# Revit family: M_Plug Valve - 3 Way - Lever Handle - 50-100 mm
name_source: partatom
category: Pipe Accessories
revit_build: Autodesk Revit MEP 2014 (Build: 20130308_1515(x64)
units: mm (PartAtom-declared; Revit-internal decimal feet)

## types (4) — shared parameters
Valve Material = PVC, Green

## per-type parameters (varying)
| type | Axis Height | Flange Diameter | Flange Radius | H2 | H3 | Height 1 | Height 2 | Height 3 | K Coefficient | Length 1 | Length 2 | Lever Length | Nominal Radius | Open Height | Outside Diameter | Outside Radius | Radius 1 | Valve Length | Width 1 |
| 50 mm | 114 mm  [stored 0.374016 ft] | 152 mm  [stored 0.498688 ft] | 76 mm  [stored 0.249344 ft] | 119 mm | 36 mm | 76 mm  [stored 0.249344 ft] | 55 mm  [stored 0.180446 ft] | 28 mm | 3.48 | 89 mm  [stored 0.291995 ft] | 103 mm | 457 mm  [stored 1.49934 ft] | 25 mm | 130 mm  [stored 0.426509 ft] | 55 mm | 28 mm | 26 mm | 178 mm  [stored 0.58399 ft] | 38 mm |
| 65 mm | 130 mm  [stored 0.426509 ft] | 178 mm  [stored 0.58399 ft] | 89 mm  [stored 0.291995 ft] | 135 mm | 41 mm | 89 mm  [stored 0.291995 ft] | 72 mm | 36 mm | 3.59 | 102 mm | 117 mm | 610 mm  [stored 2.00131 ft] | 33 mm | 145 mm  [stored 0.475722 ft] | 72 mm | 36 mm | 29 mm | 203 mm  [stored 0.66601 ft] | 49 mm |
| 80 mm | 130 mm  [stored 0.426509 ft] | 191 mm  [stored 0.62664 ft] | 96 mm | 135 mm | 41 mm | 95 mm | 88 mm | 44 mm | 8.76 | 102 mm | 117 mm | 610 mm  [stored 2.00131 ft] | 40 mm | 145 mm  [stored 0.475722 ft] | 88 mm | 44 mm | 29 mm | 203 mm  [stored 0.66601 ft] | 60 mm  [stored 0.19685 ft] |
| 100 mm | 152 mm  [stored 0.498688 ft] | 229 mm | 115 mm | 153 mm | 46 mm | 114 mm  [stored 0.374016 ft] | 110 mm  [stored 0.360892 ft] | 55 mm  [stored 0.180446 ft] | 8.51 | 115 mm | 132 mm | 762 mm  [stored 2.5 ft] | 50 mm | 178 mm  [stored 0.58399 ft] | 110 mm | 55 mm  [stored 0.180446 ft] | 33 mm | 229 mm | 75 mm  [stored 0.246063 ft] |

note: column(s) folded — value = type name in every type: Nominal Diameter

note: [stored X ft] marks values corroborated as IEEE doubles in the binary element streams (Revit-internal decimal feet)

## geometry (parser evidence)
native form markers: Blend x2, Sweep x1
no freeform markers — native parametric forms only
